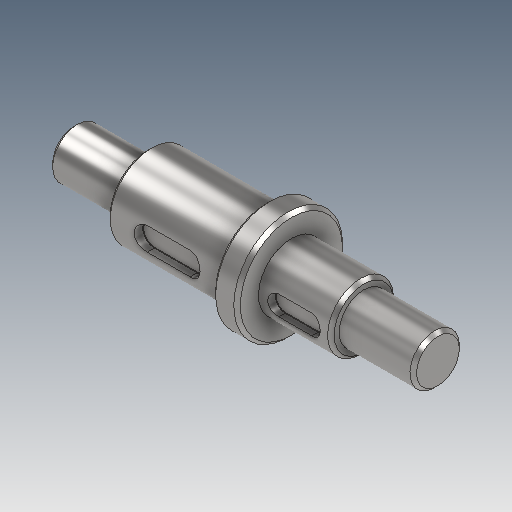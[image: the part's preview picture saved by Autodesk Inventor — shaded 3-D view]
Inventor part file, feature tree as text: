
AUTODESK INVENTOR PART (.ipt)
format: ipt  version: 2025 (Build 290162000, 162)  size: 276,992 bytes
history: native  units: mm
features: chamfer x6, other x4, revolve x1
ambient origin geometry x6: Origin, XZ Plane, XY Plane, X Axis, Y Axis, Z Axis
bodies: 实体1 (feature_tree)
feature tree (11):
  revolve  "旋转1"  [1 undecoded]
  chamfer  "倒角6"  Distance=30.0mm
  chamfer  "倒角7"  Distance=50.0mm
  chamfer  "倒角1"  Distance=66.0mm
  chamfer  "倒角2"  Distance=40.0mm
  chamfer  "倒角3"  Distance=30.0mm
  chamfer  "倒角5"  [1 undecoded]
  other  "轴键槽"
  other  "轴键槽2"
  other  "起始平面"
  other  "主草图"
note: 2 required parameter values undecoded (feature->parameter linkage not recoverable at this tier; creation-order binding heuristic only, values carry confidence <= 0.55)